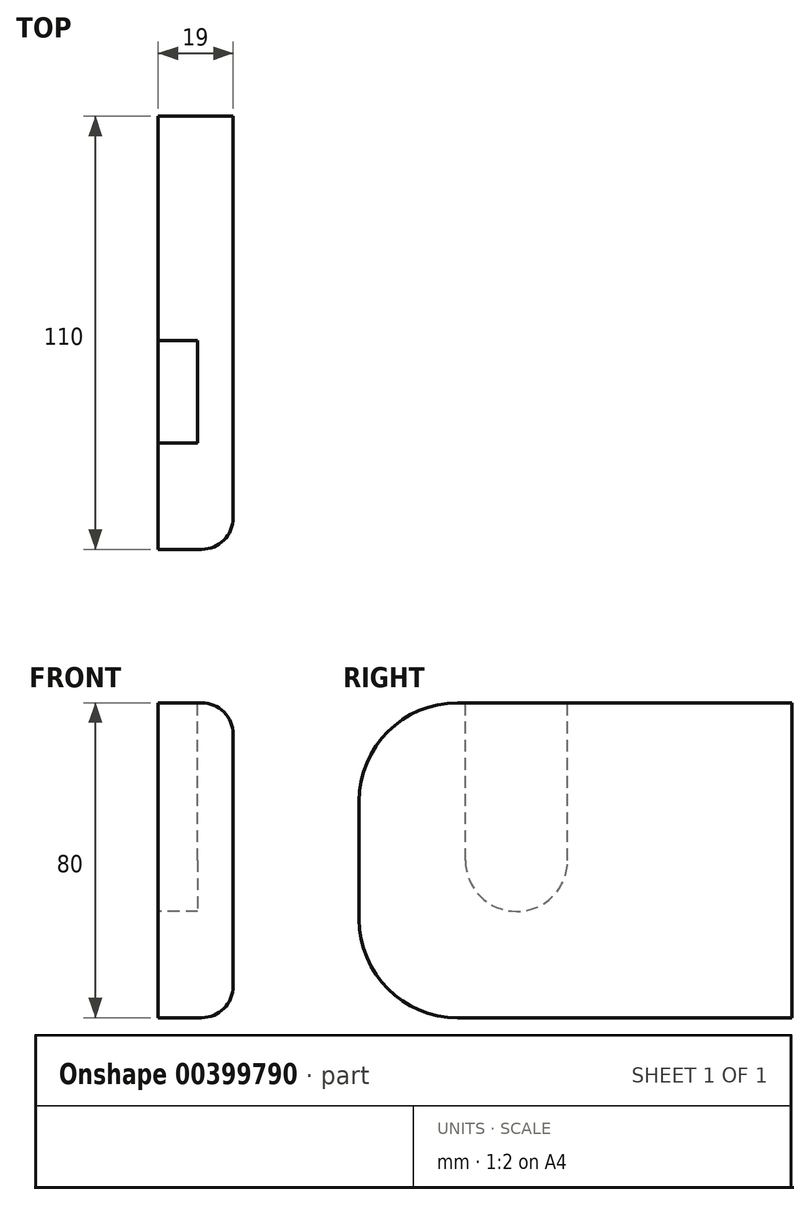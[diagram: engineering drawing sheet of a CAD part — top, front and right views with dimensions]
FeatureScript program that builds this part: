
annotation { "Feature Type Name" : "Feature", "Feature Type Description" : "" }
export const myFeature = defineFeature(function(context is Context, id is Id, definition is map)
    precondition{}
    {
        {
            var Q0;
            Q0=qCreatedBy(makeId("Right.planeOp"),FACE);
            var sketch = newSketch(context, id + "F0", { "sketchPlane" : qUnion([Q0])});
            skLineSegment(sketch, "E0", {"start": v(0, 0) * mm, "end": v(-85, 0) * mm});
            skLineSegment(sketch, "E1", {"start": v(-110, 25) * mm, "end": v(-110, 55) * mm});
            skLineSegment(sketch, "E2", {"start": v(-85, 80) * mm, "end": v(0, 80) * mm});
            skLineSegment(sketch, "E3", {"start": v(0, 80) * mm, "end": v(0, 0) * mm});
            skPoint(sketch, "E4.visualSharp", {"position": v(-110, 80) * mm});
            skArc(sketch, "E4.filletArc", {"start": v(-85, 80) * mm, "mid": v(-102.68, 72.68) * mm, "end": v(-110, 55) * mm});
            skPoint(sketch, "E5.visualSharp", {"position": v(-110, 0) * mm});
            skArc(sketch, "E5.filletArc", {"start": v(-110, 25) * mm, "mid": v(-102.68, 7.32) * mm, "end": v(-85, 0) * mm});
            skSolve(sketch);
        }
        {
            var Q0;
            Q0=makeQuery(id+"F0.imprint","IMPRINT",FACE,{"disambiguationData":[TD([[makeQuery(id+"F0.imprint","IMPRINT",EDGE,{"derivedFrom":sQuery(id+"F0.wireOp",EDGE,"E0")}),-1.0]])]});
            extrude(context, id + "F1", {"entities" : qUnion([Q0]), "depth" : 19 * mm});
        }
        {
            var Q0;
            Q0=makeQuery(id+"F1.opExtrude","CAP_FACE",FACE,{"disambiguationData":[OSD([sQuery(id+"F0.wireOp",EDGE,"E0"),sQuery(id+"F0.wireOp",EDGE,"E1"),sQuery(id+"F0.wireOp",EDGE,"E2"),sQuery(id+"F0.wireOp",EDGE,"E3"),sQuery(id+"F0.wireOp",EDGE,"E4.filletArc"),sQuery(id+"F0.wireOp",EDGE,"E5.filletArc")])],"isStart":true});
            var sketch = newSketch(context, id + "F2", { "sketchPlane" : qUnion([Q0])});
            skLineSegment(sketch, "E6", {"start": v(110, 40) * mm, "end": v(70, 40) * mm, "construction": true});
            skCircle(sketch, "E7", {"center": v(70, 40) * mm, "radius": 13 * mm, "construction": true});
            skArc(sketch, "E8", {"start": v(57, 40) * mm, "mid": v(70, 27) * mm, "end": v(83, 40) * mm});
            skLineSegment(sketch, "E9", {"start": v(57, 40) * mm, "end": v(57, 80) * mm});
            skLineSegment(sketch, "E10", {"start": v(83, 40) * mm, "end": v(83, 80) * mm});
            skLineSegment(sketch, "E11", {"start": v(57, 80) * mm, "end": v(83, 80) * mm});
            skSolve(sketch);
        }
        {
            var Q0;
            Q0=makeQuery(id+"F2.imprint","IMPRINT",FACE,{"disambiguationData":[TD([[makeQuery(id+"F2.imprint","IMPRINT",EDGE,{"derivedFrom":sQuery(id+"F2.wireOp",EDGE,"E8")}),1.0]])]});
            extrude(context, id + "F3", {"entities" : qUnion([Q0]), "operationType" : NewBodyOperationType.REMOVE, "oppositeDirection" : true, "depth" : 10 * mm});
        }
        {
            var Q0;
            Q0=makeQuery(id+"F1.opExtrude","CAP_EDGE",EDGE,{"disambiguationData":[OSD([sQuery(id+"F0.wireOp",EDGE,"E2")])],"isStart":false});
            fillet(context, id + "F4", {"entities" : qUnion([Q0]), "radius" : 8 * mm, "tangentPropagation" : true, "allowEdgeOverflow" : false});
        }
    });
